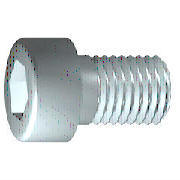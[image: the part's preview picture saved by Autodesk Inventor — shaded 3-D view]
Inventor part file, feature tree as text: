
AUTODESK INVENTOR PART (.ipt)
format: ipt  version: 2020 (Build 240168000, 168)  size: 186,880 bytes
history: native  units: mm (DEFAULTED — no unit token found)
features: sketch x2, other x1, extrude x1, plane x1, fillet x1
ambient origin geometry x7: Origin, YZ Plane, XY Plane, X Axis, Y Axis, Z Axis, Center Point
bodies: Solid1 (feature_tree)
feature tree (6):
  other  "Bryła"
  extrude  "Szczelina"  Depth=22.0mm
  plane  "Work Plane1"
  fillet  "Fillet2"  Radius=0.49086mm
  sketch  "Szkic1"
  sketch  "Szkic2"
